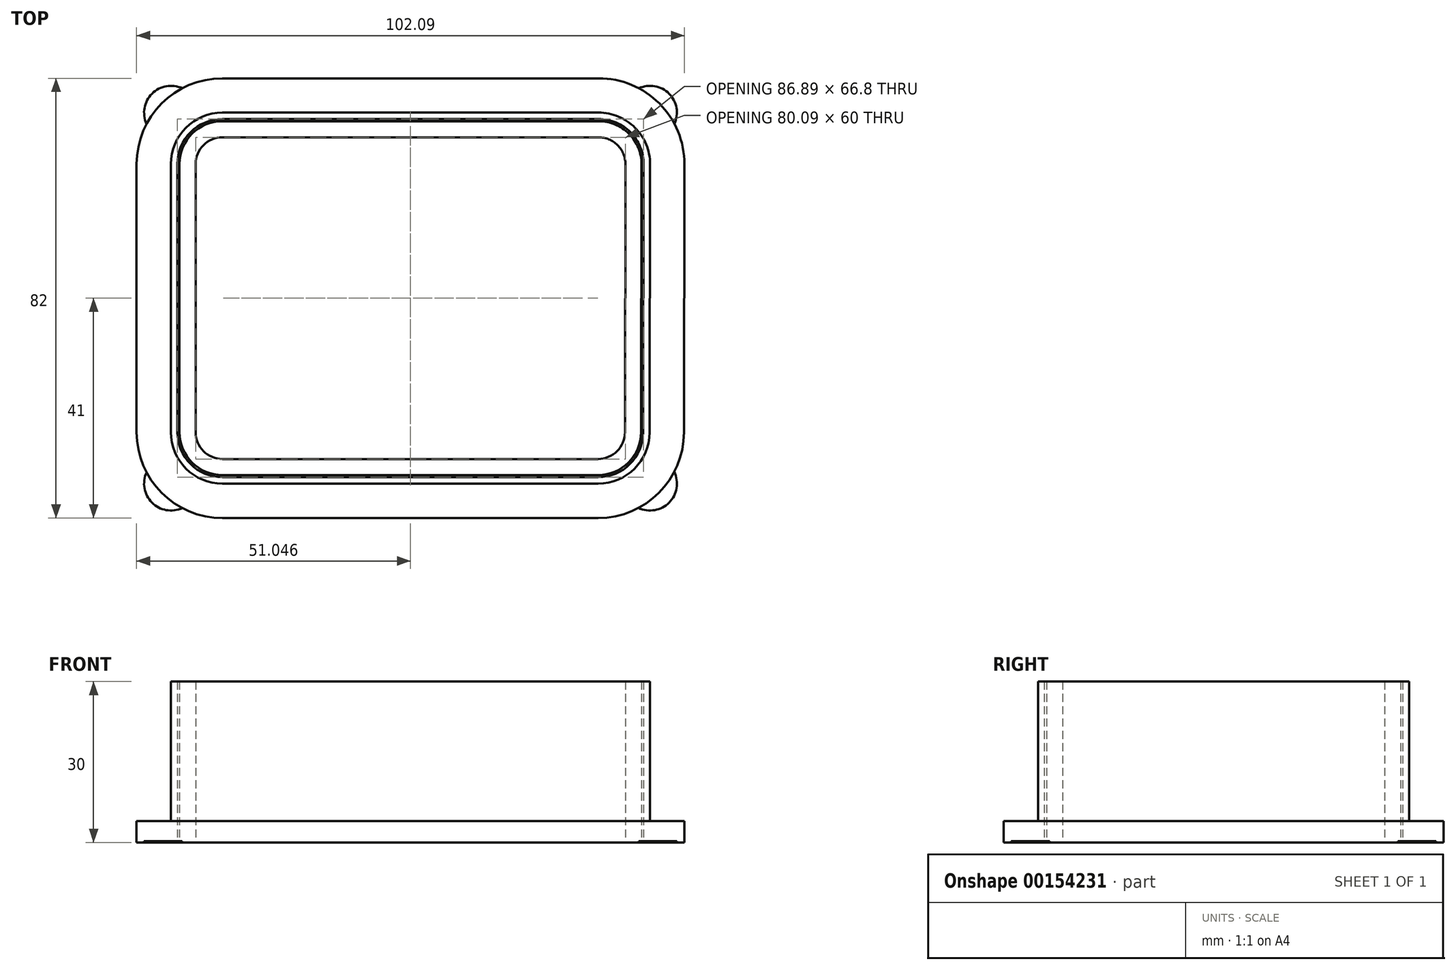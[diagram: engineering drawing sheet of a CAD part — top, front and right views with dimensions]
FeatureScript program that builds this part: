
annotation { "Feature Type Name" : "Feature", "Feature Type Description" : "" }
export const myFeature = defineFeature(function(context is Context, id is Id, definition is map)
    precondition{}
    {
        {
            var Q0;
            Q0=qCreatedBy(makeId("Top.planeOp"),FACE);
            var sketch = newSketch(context, id + "F0", { "sketchPlane" : qUnion([Q0])});
            skLineSegment(sketch, "E0.bottom", {"start": v(-35.1, -30) * mm, "end": v(34.9, -30) * mm});
            skLineSegment(sketch, "E0.top", {"start": v(-35.1, 30) * mm, "end": v(35, 30) * mm});
            skLineSegment(sketch, "E0.left", {"start": v(-40.1, -25) * mm, "end": v(-40.1, 25) * mm});
            skLineSegment(sketch, "E1", {"start": v(40, 25) * mm, "end": v(39.9, -25) * mm});
            skPoint(sketch, "E2.visualSharp", {"position": v(-40.1, 30) * mm});
            skArc(sketch, "E2.filletArc", {"start": v(-35.1, 30) * mm, "mid": v(-38.64, 28.54) * mm, "end": v(-40.1, 25) * mm});
            skPoint(sketch, "E3.visualSharp", {"position": v(40, 30) * mm});
            skArc(sketch, "E3.filletArc", {"start": v(40, 25) * mm, "mid": v(38.53, 28.53) * mm, "end": v(35, 30) * mm});
            skPoint(sketch, "E4.visualSharp", {"position": v(39.9, -30) * mm});
            skArc(sketch, "E4.filletArc", {"start": v(34.9, -30) * mm, "mid": v(38.44, -28.54) * mm, "end": v(39.9, -25) * mm});
            skPoint(sketch, "E5.visualSharp", {"position": v(-40.1, -30) * mm});
            skArc(sketch, "E5.filletArc", {"start": v(-40.1, -25) * mm, "mid": v(-38.64, -28.54) * mm, "end": v(-35.1, -30) * mm});
            skArc(sketch, "E6.0", {"start": v(-35.1, 33) * mm, "mid": v(-40.76, 30.66) * mm, "end": v(-43.1, 25) * mm});
            skLineSegment(sketch, "E6.1", {"start": v(-43.1, -25) * mm, "end": v(-43.1, 25) * mm});
            skLineSegment(sketch, "E6.2", {"start": v(-35.1, 33) * mm, "end": v(35, 33) * mm});
            skArc(sketch, "E6.3", {"start": v(-43.1, -25) * mm, "mid": v(-40.76, -30.66) * mm, "end": v(-35.1, -33) * mm});
            skArc(sketch, "E6.4", {"start": v(43, 24.99) * mm, "mid": v(40.65, 30.65) * mm, "end": v(35, 33) * mm});
            skLineSegment(sketch, "E6.5", {"start": v(43, 24.99) * mm, "end": v(42.9, -25.01) * mm});
            skArc(sketch, "E6.6", {"start": v(34.9, -33) * mm, "mid": v(40.56, -30.66) * mm, "end": v(42.9, -25.01) * mm});
            skLineSegment(sketch, "E6.7", {"start": v(-35.1, -33) * mm, "end": v(34.9, -33) * mm});
            skArc(sketch, "E7.0", {"start": v(-35.1, 33.4) * mm, "mid": v(-41.04, 30.94) * mm, "end": v(-43.5, 25) * mm});
            skLineSegment(sketch, "E7.1", {"start": v(-43.5, -25) * mm, "end": v(-43.5, 25) * mm});
            skLineSegment(sketch, "E7.2", {"start": v(-35.1, 33.4) * mm, "end": v(35, 33.4) * mm});
            skArc(sketch, "E7.3", {"start": v(-43.5, -25) * mm, "mid": v(-41.04, -30.94) * mm, "end": v(-35.1, -33.4) * mm});
            skArc(sketch, "E7.4", {"start": v(43.4, 24.99) * mm, "mid": v(40.94, 30.93) * mm, "end": v(35, 33.4) * mm});
            skLineSegment(sketch, "E7.5", {"start": v(43.4, 24.99) * mm, "end": v(43.3, -25.01) * mm});
            skArc(sketch, "E7.6", {"start": v(34.9, -33.4) * mm, "mid": v(40.84, -30.94) * mm, "end": v(43.3, -25.01) * mm});
            skLineSegment(sketch, "E7.7", {"start": v(-35.1, -33.4) * mm, "end": v(34.9, -33.4) * mm});
            skArc(sketch, "E8.0", {"start": v(-35.1, 34.6) * mm, "mid": v(-41.89, 31.79) * mm, "end": v(-44.7, 25) * mm});
            skLineSegment(sketch, "E8.1", {"start": v(-44.7, -25) * mm, "end": v(-44.7, 25) * mm});
            skLineSegment(sketch, "E8.2", {"start": v(-35.1, 34.6) * mm, "end": v(35, 34.6) * mm});
            skArc(sketch, "E8.3", {"start": v(-44.7, -25) * mm, "mid": v(-41.89, -31.79) * mm, "end": v(-35.1, -34.6) * mm});
            skArc(sketch, "E8.4", {"start": v(44.6, 24.98) * mm, "mid": v(41.79, 31.78) * mm, "end": v(35, 34.6) * mm});
            skLineSegment(sketch, "E8.5", {"start": v(44.6, 24.98) * mm, "end": v(44.5, -25.02) * mm});
            skArc(sketch, "E8.6", {"start": v(34.9, -34.6) * mm, "mid": v(41.7, -31.8) * mm, "end": v(44.5, -25.02) * mm});
            skLineSegment(sketch, "E8.7", {"start": v(-35.1, -34.6) * mm, "end": v(34.9, -34.6) * mm});
            skLineSegment(sketch, "E9", {"start": v(-44.7, 34.6) * mm, "end": v(44.6, 34.6) * mm, "construction": true});
            skLineSegment(sketch, "E10", {"start": v(44.6, 34.6) * mm, "end": v(44.6, -34.6) * mm, "construction": true});
            skLineSegment(sketch, "E11", {"start": v(44.6, -34.6) * mm, "end": v(-44.7, -34.6) * mm, "construction": true});
            skLineSegment(sketch, "E12", {"start": v(-44.7, -34.6) * mm, "end": v(-44.7, 34.6) * mm, "construction": true});
            skCircle(sketch, "E13", {"center": v(-44.7, 34.6) * mm, "radius": 5 * mm});
            skCircle(sketch, "E14", {"center": v(44.6, 34.6) * mm, "radius": 5 * mm});
            skCircle(sketch, "E15", {"center": v(44.6, -34.6) * mm, "radius": 5 * mm});
            skCircle(sketch, "E16", {"center": v(-44.7, -34.6) * mm, "radius": 5 * mm});
            skSolve(sketch);
        }
        {
            var Q0;
            Q0=makeQuery(id+"F0.imprint","IMPRINT",FACE,{"disambiguationData":[TD([[makeQuery(id+"F0.imprint","IMPRINT",EDGE,{"derivedFrom":sQuery(id+"F0.wireOp",EDGE,"E0.bottom")}),-1.0]])]});
            extrude(context, id + "F1", {"entities" : qUnion([Q0]), "depth" : 30 * mm});
        }
        {
            var Q0;
            {var subQ0=sQuery(id+"F0.wireOp",EDGE,"E13");var subQ1=sQuery(id+"F0.wireOp",EDGE,"E8.0");var subQ2=makeQuery(id+"F0.imprint","INTERSECT",VERTEX,{"disambiguationData":[OD(0.0)],"derivedFrom":[subQ1,subQ0]});Q0=makeQuery(id+"F0.imprint","IMPRINT",FACE,{"disambiguationData":[TD([[makeQuery(id+"F0.imprint","IMPRINT",EDGE,{"disambiguationData":[TD([[subQ2,-1.0]])],"derivedFrom":subQ1}),1.0]])]});}
            var Q1;
            {var subQ0=sQuery(id+"F0.wireOp",EDGE,"E16");var subQ1=sQuery(id+"F0.wireOp",EDGE,"E8.3");var subQ2=makeQuery(id+"F0.imprint","INTERSECT",VERTEX,{"disambiguationData":[OD(0.0)],"derivedFrom":[subQ1,subQ0]});Q1=makeQuery(id+"F0.imprint","IMPRINT",FACE,{"disambiguationData":[TD([[makeQuery(id+"F0.imprint","IMPRINT",EDGE,{"disambiguationData":[TD([[subQ2,-1.0]])],"derivedFrom":subQ1}),1.0]])]});}
            var Q2;
            {var subQ0=sQuery(id+"F0.wireOp",EDGE,"E14");var subQ1=sQuery(id+"F0.wireOp",EDGE,"E8.4");var subQ2=makeQuery(id+"F0.imprint","INTERSECT",VERTEX,{"disambiguationData":[OD(0.0)],"derivedFrom":[subQ1,subQ0]});Q2=makeQuery(id+"F0.imprint","IMPRINT",FACE,{"disambiguationData":[TD([[makeQuery(id+"F0.imprint","IMPRINT",EDGE,{"disambiguationData":[TD([[subQ2,-1.0]])],"derivedFrom":subQ1}),1.0]])]});}
            var Q3;
            {var subQ0=sQuery(id+"F0.wireOp",EDGE,"E15");var subQ1=sQuery(id+"F0.wireOp",EDGE,"E8.6");var subQ2=makeQuery(id+"F0.imprint","INTERSECT",VERTEX,{"disambiguationData":[OD(0.0)],"derivedFrom":[subQ1,subQ0]});Q3=makeQuery(id+"F0.imprint","IMPRINT",FACE,{"disambiguationData":[TD([[makeQuery(id+"F0.imprint","IMPRINT",EDGE,{"disambiguationData":[TD([[subQ2,-1.0]])],"derivedFrom":subQ1}),1.0]])]});}
            var Q4;
            Q4=makeQuery(id+"F0.imprint","IMPRINT",FACE,{"disambiguationData":[TD([[makeQuery(id+"F0.imprint","IMPRINT",EDGE,{"derivedFrom":sQuery(id+"F0.wireOp",EDGE,"E7.0")}),-1.0]])]});
            extrude(context, id + "F2", {"entities" : qUnion([Q0, Q1, Q2, Q3, Q4]), "depth" : 30 * mm});
        }
        {
            var Q0;
            Q0=makeQuery(id+"F2.opExtrude","CAP_FACE",FACE,{"disambiguationData":[OSD([sQuery(id+"F0.wireOp",EDGE,"E7.0"),sQuery(id+"F0.wireOp",EDGE,"E7.1"),sQuery(id+"F0.wireOp",EDGE,"E7.2"),sQuery(id+"F0.wireOp",EDGE,"E7.3"),sQuery(id+"F0.wireOp",EDGE,"E7.4"),sQuery(id+"F0.wireOp",EDGE,"E7.5"),sQuery(id+"F0.wireOp",EDGE,"E7.6"),sQuery(id+"F0.wireOp",EDGE,"E7.7"),sQuery(id+"F0.wireOp",EDGE,"E8.0"),sQuery(id+"F0.wireOp",EDGE,"E8.1"),sQuery(id+"F0.wireOp",EDGE,"E8.2"),sQuery(id+"F0.wireOp",EDGE,"E8.3"),sQuery(id+"F0.wireOp",EDGE,"E8.4"),sQuery(id+"F0.wireOp",EDGE,"E8.5"),sQuery(id+"F0.wireOp",EDGE,"E8.6"),sQuery(id+"F0.wireOp",EDGE,"E8.7")])],"isStart":true});
            var sketch = newSketch(context, id + "F3", { "sketchPlane" : qUnion([Q0])});
            skLineSegment(sketch, "E17.0", {"start": v(-51.1, 25) * mm, "end": v(-51.1, -25) * mm});
            skArc(sketch, "E17.1", {"start": v(-35.1, -41) * mm, "mid": v(-46.41, -36.31) * mm, "end": v(-51.1, -25) * mm});
            skArc(sketch, "E17.2", {"start": v(-51.1, 25) * mm, "mid": v(-46.41, 36.31) * mm, "end": v(-35.1, 41) * mm});
            skLineSegment(sketch, "E17.3", {"start": v(-35.1, -41) * mm, "end": v(35, -41) * mm});
            skLineSegment(sketch, "E17.4", {"start": v(-35.1, 41) * mm, "end": v(34.9, 41) * mm});
            skArc(sketch, "E17.5", {"start": v(34.9, 41) * mm, "mid": v(46.21, 36.32) * mm, "end": v(50.9, 25.03) * mm});
            skLineSegment(sketch, "E17.6", {"start": v(51, -24.97) * mm, "end": v(50.9, 25.03) * mm});
            skArc(sketch, "E17.7", {"start": v(51, -24.97) * mm, "mid": v(46.31, -36.3) * mm, "end": v(35, -41) * mm});
            skSolve(sketch);
        }
        {
            var Q0;
            Q0=makeQuery(id+"F3.imprint","IMPRINT",FACE,{"disambiguationData":[TD([[makeQuery(id+"F3.imprint","IMPRINT",EDGE,{"derivedFrom":sQuery(id+"F3.wireOp",EDGE,"E17.0")}),1.0]])]});
            extrude(context, id + "F4", {"entities" : qUnion([Q0]), "operationType" : NewBodyOperationType.ADD, "oppositeDirection" : true, "depth" : 4 * mm});
        }
        {
            var Q0;
            {var subQ0=sQuery(id+"F0.wireOp",EDGE,"E13");var subQ1=sQuery(id+"F0.wireOp",EDGE,"E8.0");var subQ2=makeQuery(id+"F0.imprint","INTERSECT",VERTEX,{"disambiguationData":[OD(0.0)],"derivedFrom":[subQ1,subQ0]});Q0=makeQuery(id+"F0.imprint","IMPRINT",FACE,{"disambiguationData":[TD([[makeQuery(id+"F0.imprint","IMPRINT",EDGE,{"disambiguationData":[TD([[subQ2,-1.0]])],"derivedFrom":subQ1}),-1.0]])]});}
            var Q1;
            {var subQ0=sQuery(id+"F0.wireOp",EDGE,"E16");var subQ1=sQuery(id+"F0.wireOp",EDGE,"E8.3");var subQ2=makeQuery(id+"F0.imprint","INTERSECT",VERTEX,{"disambiguationData":[OD(0.0)],"derivedFrom":[subQ1,subQ0]});Q1=makeQuery(id+"F0.imprint","IMPRINT",FACE,{"disambiguationData":[TD([[makeQuery(id+"F0.imprint","IMPRINT",EDGE,{"disambiguationData":[TD([[subQ2,-1.0]])],"derivedFrom":subQ1}),-1.0]])]});}
            var Q2;
            {var subQ0=sQuery(id+"F0.wireOp",EDGE,"E14");var subQ1=sQuery(id+"F0.wireOp",EDGE,"E8.4");var subQ2=makeQuery(id+"F0.imprint","INTERSECT",VERTEX,{"disambiguationData":[OD(0.0)],"derivedFrom":[subQ1,subQ0]});Q2=makeQuery(id+"F0.imprint","IMPRINT",FACE,{"disambiguationData":[TD([[makeQuery(id+"F0.imprint","IMPRINT",EDGE,{"disambiguationData":[TD([[subQ2,-1.0]])],"derivedFrom":subQ1}),-1.0]])]});}
            var Q3;
            {var subQ0=sQuery(id+"F0.wireOp",EDGE,"E15");var subQ1=sQuery(id+"F0.wireOp",EDGE,"E8.6");var subQ2=makeQuery(id+"F0.imprint","INTERSECT",VERTEX,{"disambiguationData":[OD(0.0)],"derivedFrom":[subQ1,subQ0]});Q3=makeQuery(id+"F0.imprint","IMPRINT",FACE,{"disambiguationData":[TD([[makeQuery(id+"F0.imprint","IMPRINT",EDGE,{"disambiguationData":[TD([[subQ2,-1.0]])],"derivedFrom":subQ1}),-1.0]])]});}
            var Q4;
            {var subQ0=sQuery(id+"F0.wireOp",EDGE,"E13");var subQ1=sQuery(id+"F0.wireOp",EDGE,"E8.0");var subQ2=makeQuery(id+"F0.imprint","INTERSECT",VERTEX,{"disambiguationData":[OD(0.0)],"derivedFrom":[subQ1,subQ0]});Q4=makeQuery(id+"F0.imprint","IMPRINT",FACE,{"disambiguationData":[TD([[makeQuery(id+"F0.imprint","IMPRINT",EDGE,{"disambiguationData":[TD([[subQ2,-1.0]])],"derivedFrom":subQ1}),1.0]])]});}
            var Q5;
            {var subQ0=sQuery(id+"F0.wireOp",EDGE,"E16");var subQ1=sQuery(id+"F0.wireOp",EDGE,"E8.3");var subQ2=makeQuery(id+"F0.imprint","INTERSECT",VERTEX,{"disambiguationData":[OD(0.0)],"derivedFrom":[subQ1,subQ0]});Q5=makeQuery(id+"F0.imprint","IMPRINT",FACE,{"disambiguationData":[TD([[makeQuery(id+"F0.imprint","IMPRINT",EDGE,{"disambiguationData":[TD([[subQ2,-1.0]])],"derivedFrom":subQ1}),1.0]])]});}
            var Q6;
            {var subQ0=sQuery(id+"F0.wireOp",EDGE,"E14");var subQ1=sQuery(id+"F0.wireOp",EDGE,"E8.4");var subQ2=makeQuery(id+"F0.imprint","INTERSECT",VERTEX,{"disambiguationData":[OD(0.0)],"derivedFrom":[subQ1,subQ0]});Q6=makeQuery(id+"F0.imprint","IMPRINT",FACE,{"disambiguationData":[TD([[makeQuery(id+"F0.imprint","IMPRINT",EDGE,{"disambiguationData":[TD([[subQ2,-1.0]])],"derivedFrom":subQ1}),1.0]])]});}
            var Q7;
            {var subQ0=sQuery(id+"F0.wireOp",EDGE,"E15");var subQ1=sQuery(id+"F0.wireOp",EDGE,"E8.6");var subQ2=makeQuery(id+"F0.imprint","INTERSECT",VERTEX,{"disambiguationData":[OD(0.0)],"derivedFrom":[subQ1,subQ0]});Q7=makeQuery(id+"F0.imprint","IMPRINT",FACE,{"disambiguationData":[TD([[makeQuery(id+"F0.imprint","IMPRINT",EDGE,{"disambiguationData":[TD([[subQ2,-1.0]])],"derivedFrom":subQ1}),1.0]])]});}
            extrude(context, id + "F5", {"entities" : qUnion([Q0, Q1, Q2, Q3, Q4, Q5, Q6, Q7]), "operationType" : NewBodyOperationType.ADD, "depth" : 0.2 * mm});
        }
    });
